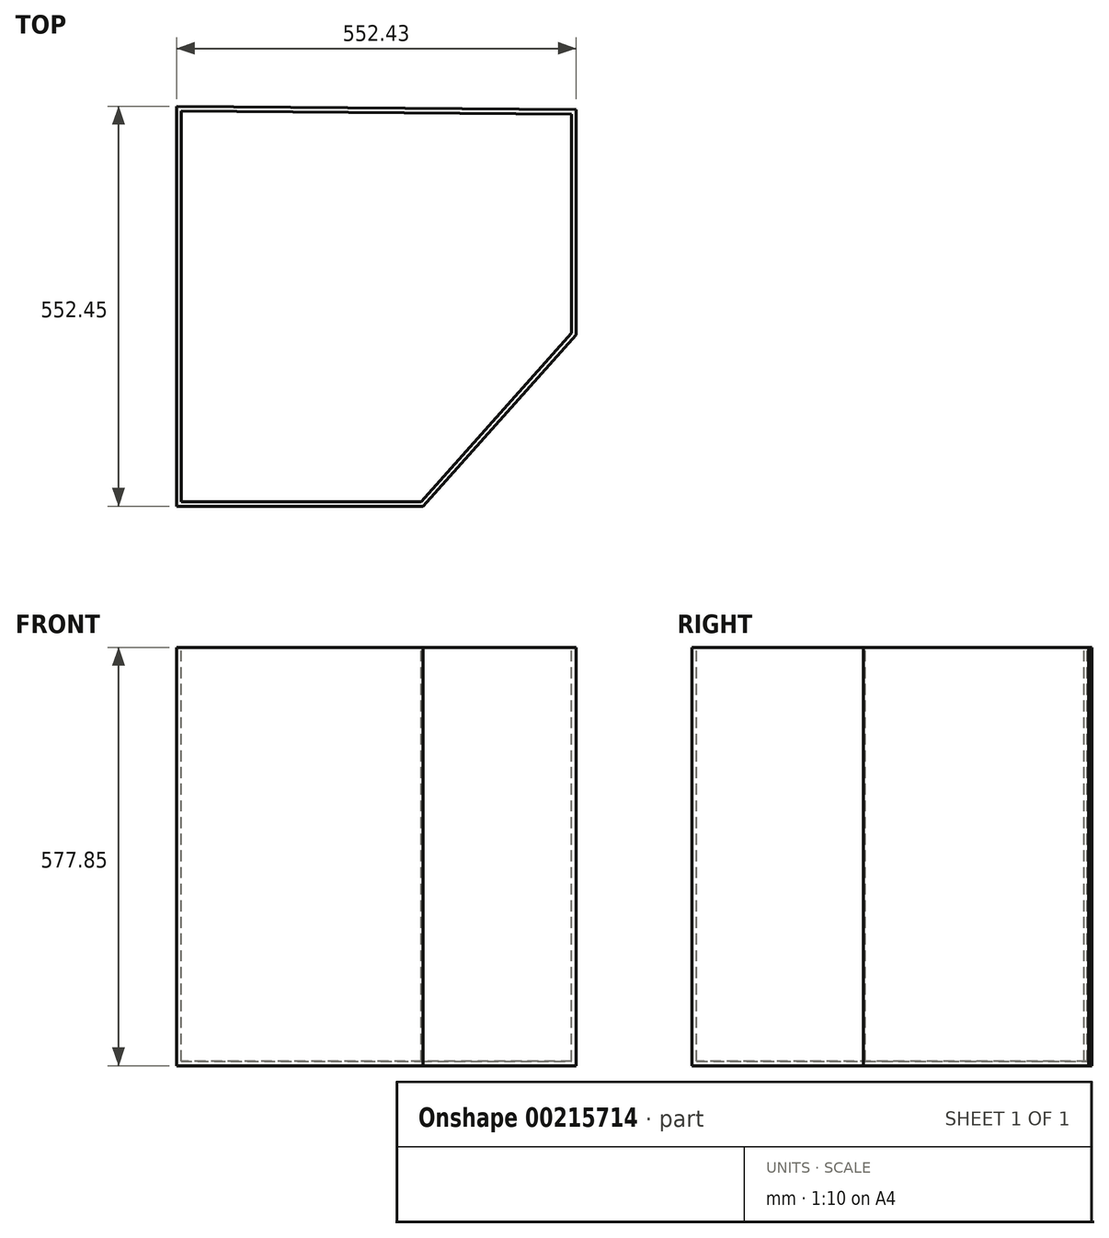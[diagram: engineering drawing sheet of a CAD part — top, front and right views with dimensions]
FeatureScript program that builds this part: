
annotation { "Feature Type Name" : "Feature", "Feature Type Description" : "" }
export const myFeature = defineFeature(function(context is Context, id is Id, definition is map)
    precondition{}
    {
        {
            var Q0;
            Q0=qCreatedBy(makeId("Top.planeOp"),FACE);
            var sketch = newSketch(context, id + "F0", { "sketchPlane" : qUnion([Q0])});
            skLineSegment(sketch, "E0", {"start": v(-227.3, 277.1) * mm, "end": v(-227.3, -275.35) * mm});
            skLineSegment(sketch, "E1", {"start": v(-227.3, -275.35) * mm, "end": v(113.35, -275.35) * mm});
            skLineSegment(sketch, "E2", {"start": v(113.35, -275.35) * mm, "end": v(325.12, -38.8) * mm});
            skLineSegment(sketch, "E3", {"start": v(325.12, -38.8) * mm, "end": v(325.12, 272.39) * mm});
            skLineSegment(sketch, "E4", {"start": v(325.12, 272.39) * mm, "end": v(-227.3, 277.1) * mm});
            skSolve(sketch);
        }
        {
            var Q0;
            Q0 = qSketchRegion(id + "F0", true);
            extrude(context, id + "F1", {"entities" : qUnion([Q0]), "depth" : 577.85 * mm});
        }
        {
            var Q0;
            Q0=makeQuery(id+"F1.opExtrude","CAP_FACE",FACE,{"disambiguationData":[OSD([sQuery(id+"F0.wireOp",EDGE,"E0"),sQuery(id+"F0.wireOp",EDGE,"E1"),sQuery(id+"F0.wireOp",EDGE,"E2"),sQuery(id+"F0.wireOp",EDGE,"E3"),sQuery(id+"F0.wireOp",EDGE,"E4")])],"isStart":false});
            var sketch = newSketch(context, id + "F2", { "sketchPlane" : qUnion([Q0])});
            skLineSegment(sketch, "E5.0", {"start": v(110.51, -269) * mm, "end": v(318.77, -36.37) * mm});
            skLineSegment(sketch, "E5.1", {"start": v(-220.96, -269) * mm, "end": v(110.51, -269) * mm});
            skLineSegment(sketch, "E5.2", {"start": v(318.77, -36.37) * mm, "end": v(318.77, 266.1) * mm});
            skLineSegment(sketch, "E5.3", {"start": v(318.77, 266.1) * mm, "end": v(-220.96, 270.7) * mm});
            skLineSegment(sketch, "E5.4", {"start": v(-220.96, 270.7) * mm, "end": v(-220.96, -269) * mm});
            skSolve(sketch);
        }
        {
            var Q0;
            Q0 = qSketchRegion(id + "F2", true);
            extrude(context, id + "F3", {"entities" : qUnion([Q0]), "operationType" : NewBodyOperationType.REMOVE, "oppositeDirection" : true, "depth" : 571.5 * mm});
        }
    });
